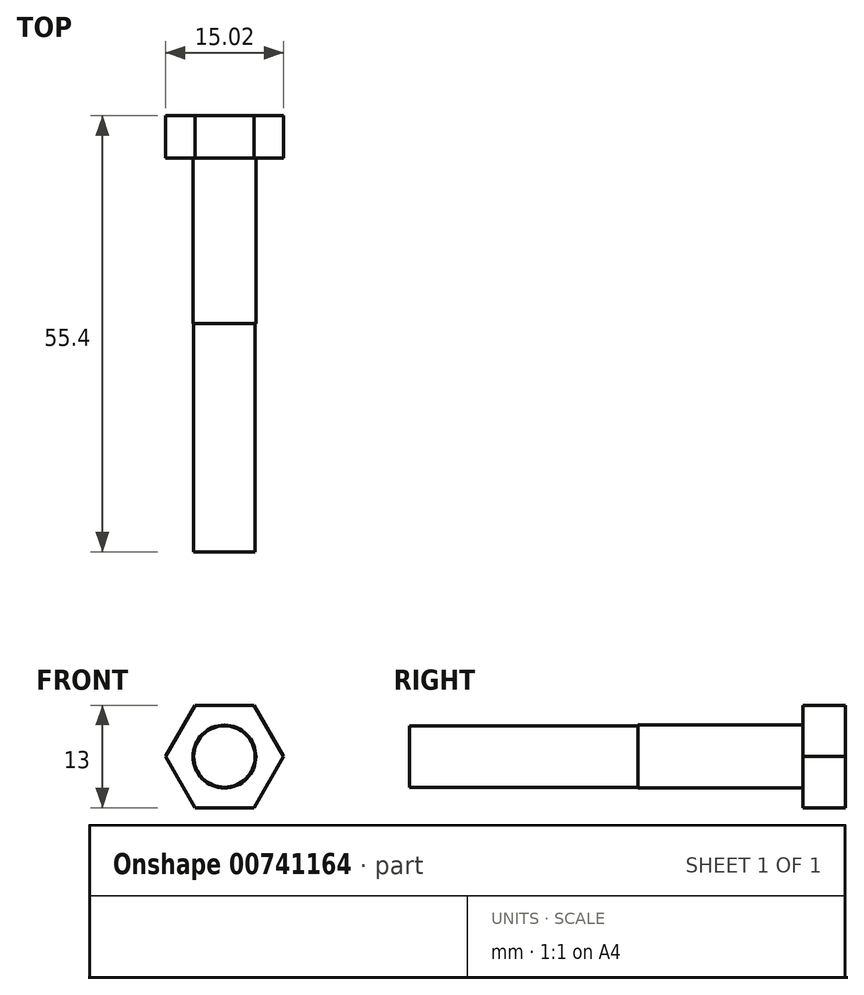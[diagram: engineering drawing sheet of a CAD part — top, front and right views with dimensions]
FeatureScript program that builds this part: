
annotation { "Feature Type Name" : "Feature", "Feature Type Description" : "" }
export const myFeature = defineFeature(function(context is Context, id is Id, definition is map)
    precondition{}
    {
        {
            var Q0;
            Q0=qCreatedBy(makeId("Front.planeOp"),FACE);
            var sketch = newSketch(context, id + "F0", { "sketchPlane" : qUnion([Q0])});
            skCircle(sketch, "E0", {"center": v(0, 0) * mm, "radius": 4 * mm});
            skCircle(sketch, "E1.cCircle", {"center": v(0, 0) * mm, "radius": 6.5 * mm, "construction": true});
            skLineSegment(sketch, "E1.0", {"start": v(-3.75, 6.5) * mm, "end": v(3.75, 6.5) * mm});
            skLineSegment(sketch, "E1.1", {"start": v(3.75, 6.5) * mm, "end": v(7.5, 0) * mm});
            skLineSegment(sketch, "E1.2", {"start": v(7.5, 0) * mm, "end": v(3.75, -6.5) * mm});
            skLineSegment(sketch, "E1.3", {"start": v(3.75, -6.5) * mm, "end": v(-3.75, -6.5) * mm});
            skLineSegment(sketch, "E1.4", {"start": v(-3.75, -6.5) * mm, "end": v(-7.5, 0) * mm});
            skLineSegment(sketch, "E1.5", {"start": v(-7.5, 0) * mm, "end": v(-3.75, 6.5) * mm});
            skPoint(sketch, "E1.0.midPoint", {"position": v(0, 6.5) * mm});
            skSolve(sketch);
        }
        {
            var Q0;
            Q0=makeQuery(id+"F0.imprint","IMPRINT",FACE,{"disambiguationData":[TD([[makeQuery(id+"F0.imprint","IMPRINT",EDGE,{"derivedFrom":sQuery(id+"F0.wireOp",EDGE,"E0")}),1.0]])]});
            extrude(context, id + "F1", {"entities" : qUnion([Q0]), "depth" : 50 * mm, "offsetDistance" : 25 * mm});
        }
        {
            var Q0;
            Q0=makeQuery(id+"F0.imprint","IMPRINT",FACE,{"disambiguationData":[TD([[makeQuery(id+"F0.imprint","IMPRINT",EDGE,{"derivedFrom":sQuery(id+"F0.wireOp",EDGE,"E0")}),1.0]])]});
            var Q1;
            Q1=makeQuery(id+"F0.imprint","IMPRINT",FACE,{"disambiguationData":[TD([[makeQuery(id+"F0.imprint","IMPRINT",EDGE,{"derivedFrom":sQuery(id+"F0.wireOp",EDGE,"E0")}),-1.0]])]});
            extrude(context, id + "F2", {"entities" : qUnion([Q0, Q1]), "operationType" : NewBodyOperationType.ADD, "oppositeDirection" : true, "depth" : 5.4 * mm, "offsetDistance" : 25 * mm});
        }
        {
            var Q0;
            Q0=makeQuery(id+"F1.opExtrude","CAP_FACE",FACE,{"disambiguationData":[OSD([sQuery(id+"F0.wireOp",EDGE,"E0")])],"isStart":false});
            var sketch = newSketch(context, id + "F3", { "sketchPlane" : qUnion([Q0])});
            skCircle(sketch, "E2", {"center": v(0, 0) * mm, "radius": 3.9 * mm});
            skCircle(sketch, "E3.0", {"center": v(0, 0) * mm, "radius": 4 * mm});
            skSolve(sketch);
        }
        {
            var Q0;
            Q0 = qSketchRegion(id + "F3", true);
            extrude(context, id + "F4", {"entities" : qUnion([Q0]), "operationType" : NewBodyOperationType.REMOVE, "oppositeDirection" : true, "depth" : 29 * mm, "offsetDistance" : 25 * mm});
        }
    });
